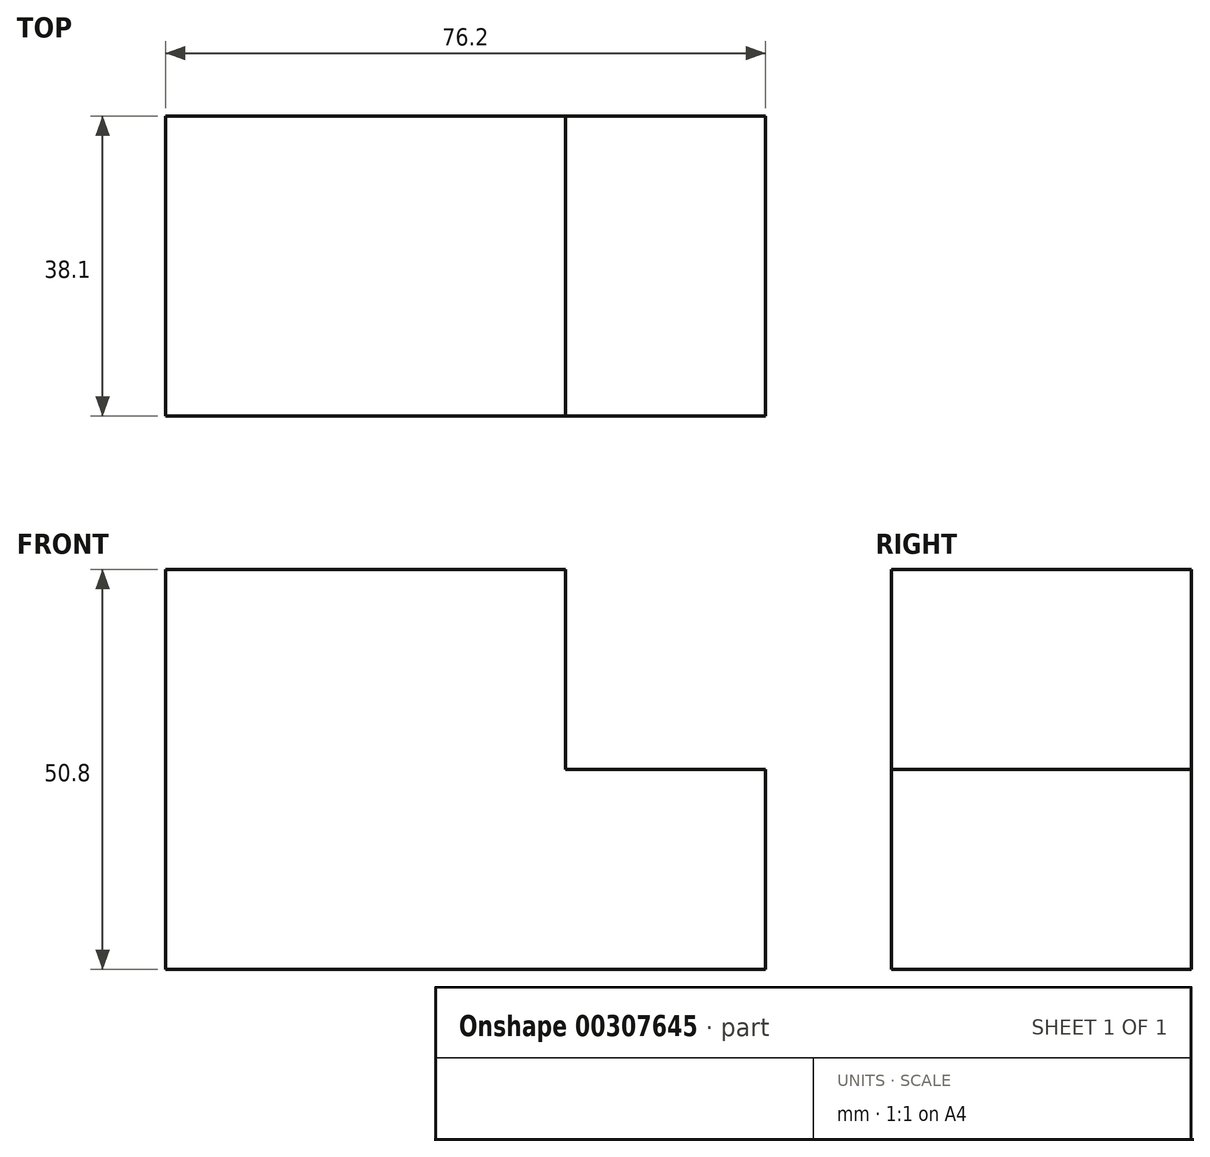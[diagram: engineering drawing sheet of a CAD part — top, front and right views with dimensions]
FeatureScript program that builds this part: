
annotation { "Feature Type Name" : "Feature", "Feature Type Description" : "" }
export const myFeature = defineFeature(function(context is Context, id is Id, definition is map)
    precondition{}
    {
        {
            var Q0;
            Q0=qCreatedBy(makeId("Front.planeOp"),FACE);
            var sketch = newSketch(context, id + "F0", { "sketchPlane" : qUnion([Q0])});
            skLineSegment(sketch, "E0", {"start": v(-39.63, -31.95) * mm, "end": v(36.57, -31.95) * mm});
            skLineSegment(sketch, "E1", {"start": v(36.57, -31.95) * mm, "end": v(36.57, -6.55) * mm});
            skLineSegment(sketch, "E2", {"start": v(36.57, -6.55) * mm, "end": v(11.17, -6.55) * mm});
            skLineSegment(sketch, "E3", {"start": v(11.17, -6.55) * mm, "end": v(11.17, 18.85) * mm});
            skLineSegment(sketch, "E4", {"start": v(11.17, 18.85) * mm, "end": v(-39.63, 18.85) * mm});
            skLineSegment(sketch, "E5", {"start": v(-39.63, -31.95) * mm, "end": v(-39.63, 18.85) * mm});
            skSolve(sketch);
        }
        {
            var Q0;
            Q0=makeQuery(id+"F0.imprint","IMPRINT",FACE,{"disambiguationData":[TD([[makeQuery(id+"F0.imprint","IMPRINT",EDGE,{"derivedFrom":sQuery(id+"F0.wireOp",EDGE,"E0")}),1.0]])]});
            extrude(context, id + "F1", {"entities" : qUnion([Q0]), "depth" : 38.1 * mm});
        }
    });
